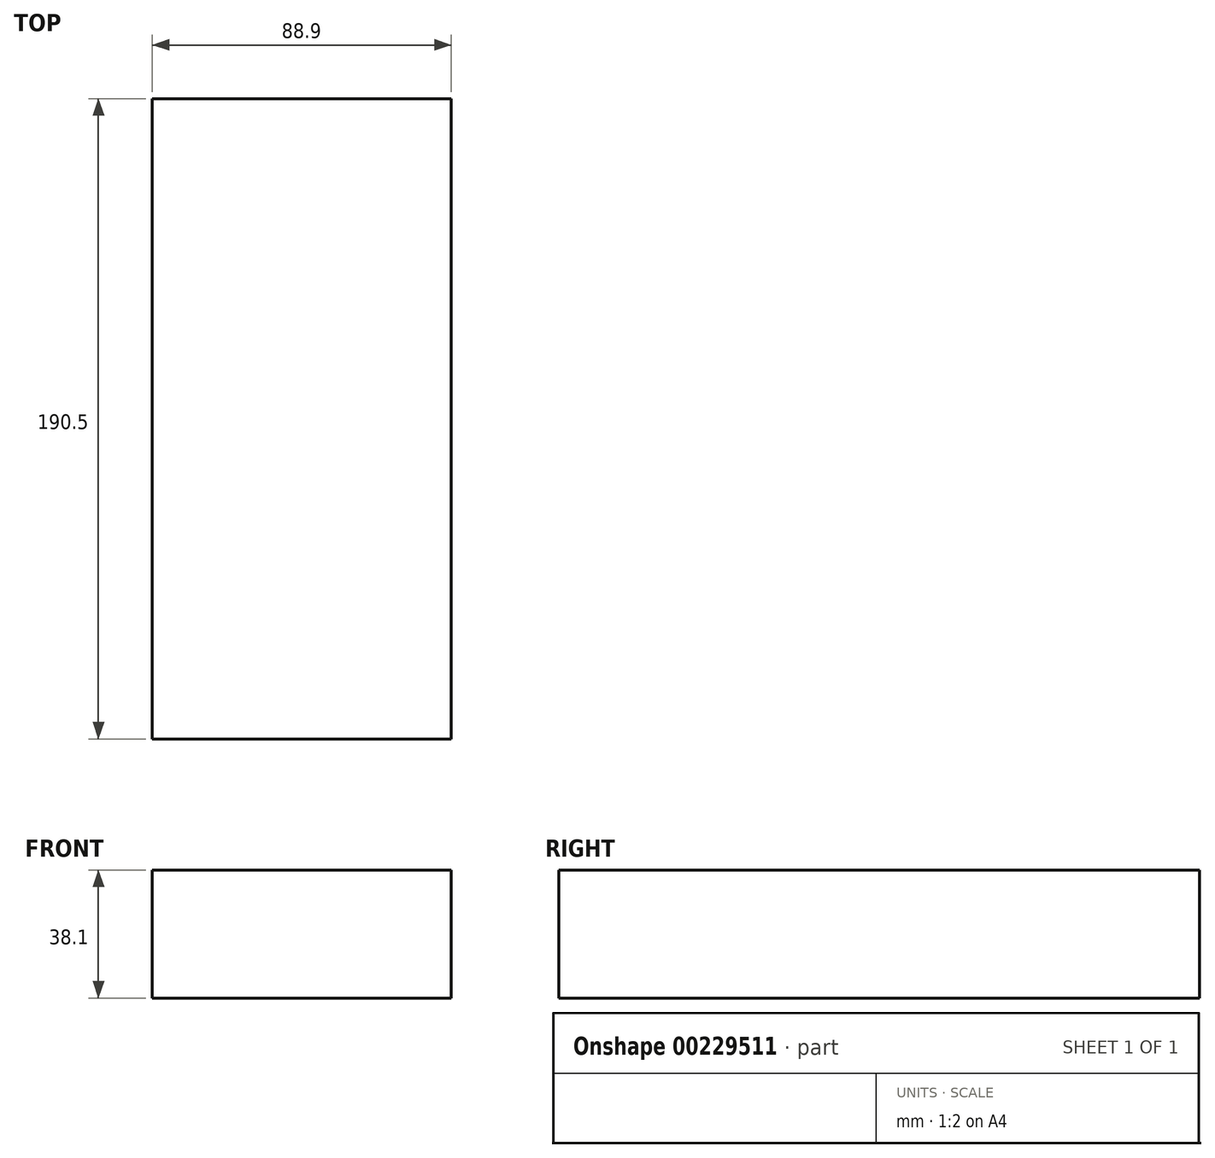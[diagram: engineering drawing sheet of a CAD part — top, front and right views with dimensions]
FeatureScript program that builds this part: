
annotation { "Feature Type Name" : "Feature", "Feature Type Description" : "" }
export const myFeature = defineFeature(function(context is Context, id is Id, definition is map)
    precondition{}
    {
        {
            var Q0;
            Q0=qCreatedBy(makeId("Front.planeOp"),FACE);
            var sketch = newSketch(context, id + "F0", { "sketchPlane" : qUnion([Q0])});
            skLineSegment(sketch, "E0.bottom", {"start": v(0, 0) * mm, "end": v(88.9, 0) * mm});
            skLineSegment(sketch, "E0.top", {"start": v(0, -38.1) * mm, "end": v(88.9, -38.1) * mm});
            skLineSegment(sketch, "E0.left", {"start": v(0, 0) * mm, "end": v(0, -38.1) * mm});
            skLineSegment(sketch, "E0.right", {"start": v(88.9, 0) * mm, "end": v(88.9, -38.1) * mm});
            skSolve(sketch);
        }
        {
            var Q0;
            Q0=qSketchRegion(id+"F0",true);
            extrude(context, id + "F1", {"entities" : qUnion([Q0]), "depth" : 190.5 * mm});
        }
    });
